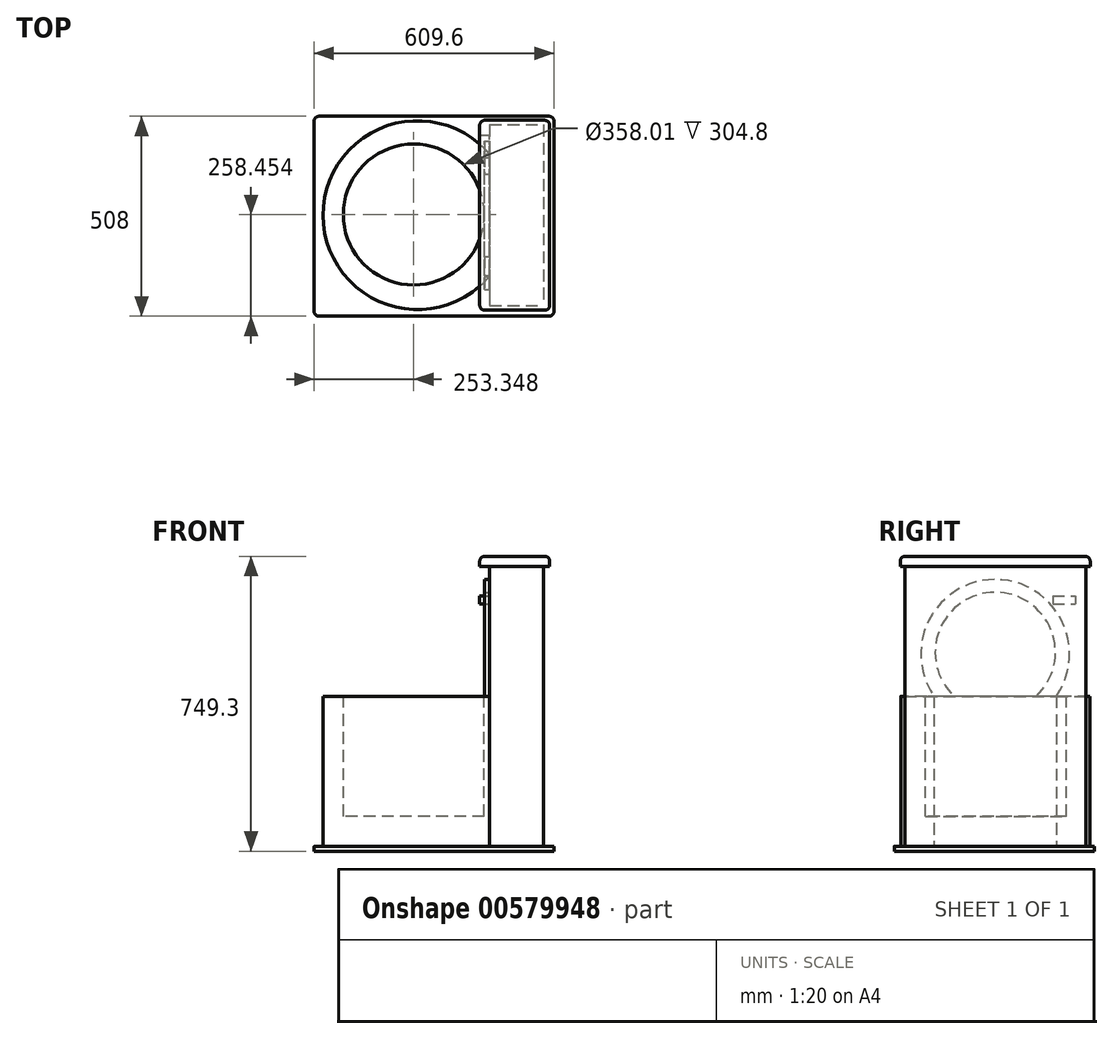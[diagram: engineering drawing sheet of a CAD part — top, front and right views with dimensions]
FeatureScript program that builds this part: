
annotation { "Feature Type Name" : "Feature", "Feature Type Description" : "" }
export const myFeature = defineFeature(function(context is Context, id is Id, definition is map)
    precondition{}
    {
        {
            var Q0;
            Q0=qCreatedBy(makeId("Top.planeOp"),FACE);
            var sketch = newSketch(context, id + "F0", { "sketchPlane" : qUnion([Q0])});
            skLineSegment(sketch, "E0.bottom", {"start": v(-336.58, 285.89) * mm, "end": v(273.02, 285.89) * mm});
            skLineSegment(sketch, "E0.top", {"start": v(-336.58, -222.11) * mm, "end": v(273.02, -222.11) * mm});
            skLineSegment(sketch, "E0.left", {"start": v(-336.58, 285.89) * mm, "end": v(-336.58, -222.11) * mm});
            skLineSegment(sketch, "E0.right", {"start": v(273.02, 285.89) * mm, "end": v(273.02, -222.11) * mm});
            skSolve(sketch);
        }
        {
            var Q0;
            Q0=makeQuery(id+"F0.imprint","IMPRINT",FACE,{"disambiguationData":[TD([[makeQuery(id+"F0.imprint","IMPRINT",EDGE,{"derivedFrom":sQuery(id+"F0.wireOp",EDGE,"E0.bottom")}),-1.0]])]});
            extrude(context, id + "F1", {"entities" : qUnion([Q0]), "depth" : 12.7 * mm, "offsetDistance" : 25.4 * mm});
        }
        {
            var Q0;
            Q0=makeQuery(id+"F1.opExtrude","CAP_FACE",FACE,{"disambiguationData":[OSD([sQuery(id+"F0.wireOp",EDGE,"E0.bottom"),sQuery(id+"F0.wireOp",EDGE,"E0.top"),sQuery(id+"F0.wireOp",EDGE,"E0.left"),sQuery(id+"F0.wireOp",EDGE,"E0.right")])],"isStart":false});
            var sketch = newSketch(context, id + "F2", { "sketchPlane" : qUnion([Q0])});
            skArc(sketch, "E1", {"start": v(109.27, 189.67) * mm, "mid": v(-313.64, 34.5) * mm, "end": v(109.27, -120.68) * mm});
            skPoint(sketch, "E1.first.point", {"position": v(-246.1, 201.36) * mm});
            skPoint(sketch, "E1.second.point", {"position": v(104.1, -126.58) * mm});
            skPoint(sketch, "E1.third.point", {"position": v(-122.1, -200.5) * mm});
            skLineSegment(sketch, "E2.bottom", {"start": v(109.27, 264.4) * mm, "end": v(245.98, 264.4) * mm});
            skLineSegment(sketch, "E2.top", {"start": v(109.27, -195.22) * mm, "end": v(245.98, -195.22) * mm});
            skLineSegment(sketch, "E2.left", {"start": v(109.27, 264.4) * mm, "end": v(109.27, 189.67) * mm});
            skLineSegment(sketch, "E2.right", {"start": v(245.98, 264.4) * mm, "end": v(245.98, -195.22) * mm});
            skLineSegment(sketch, "E3.trimOffspring", {"start": v(109.27, -120.68) * mm, "end": v(109.27, -195.22) * mm});
            skSolve(sketch);
        }
        {
            var Q0;
            Q0 = qSketchRegion(id + "F2", true);
            extrude(context, id + "F3", {"entities" : qUnion([Q0]), "operationType" : NewBodyOperationType.ADD, "depth" : 381 * mm, "offsetDistance" : 25.4 * mm});
        }
        {
            var Q0;
            Q0=makeQuery(id+"F1.opExtrude","SWEPT_EDGE",EDGE,{"disambiguationData":[OSD([sQuery(id+"F0.wireOp",EDGE,"E0.top"),sQuery(id+"F0.wireOp",EDGE,"E0.left")])]});
            var Q1;
            Q1=makeQuery(id+"F1.opExtrude","SWEPT_EDGE",EDGE,{"disambiguationData":[OSD([sQuery(id+"F0.wireOp",EDGE,"E0.top"),sQuery(id+"F0.wireOp",EDGE,"E0.right")])]});
            var Q2;
            Q2=makeQuery(id+"F1.opExtrude","SWEPT_EDGE",EDGE,{"disambiguationData":[OSD([sQuery(id+"F0.wireOp",EDGE,"E0.bottom"),sQuery(id+"F0.wireOp",EDGE,"E0.right")])]});
            var Q3;
            Q3=makeQuery(id+"F1.opExtrude","SWEPT_EDGE",EDGE,{"disambiguationData":[OSD([sQuery(id+"F0.wireOp",EDGE,"E0.bottom"),sQuery(id+"F0.wireOp",EDGE,"E0.left")])]});
            fillet(context, id + "F4", {"entities" : qUnion([Q0, Q1, Q2, Q3]), "radius" : 12.7 * mm, "tangentPropagation" : true, "allowEdgeOverflow" : false});
        }
        {
            var Q0;
            Q0=makeQuery(id+"F3.opExtrude","CAP_FACE",FACE,{"disambiguationData":[OSD([sQuery(id+"F2.wireOp",EDGE,"E1"),sQuery(id+"F2.wireOp",EDGE,"E2.bottom"),sQuery(id+"F2.wireOp",EDGE,"E2.top"),sQuery(id+"F2.wireOp",EDGE,"E2.left"),sQuery(id+"F2.wireOp",EDGE,"E2.right"),sQuery(id+"F2.wireOp",EDGE,"E3.trimOffspring")])],"isStart":false});
            var sketch = newSketch(context, id + "F5", { "sketchPlane" : qUnion([Q0])});
            skCircle(sketch, "E4", {"center": v(-83.23, 36.34) * mm, "radius": 179 * mm});
            skSolve(sketch);
        }
        {
            var Q0;
            Q0 = qSketchRegion(id + "F5", true);
            extrude(context, id + "F6", {"entities" : qUnion([Q0]), "operationType" : NewBodyOperationType.REMOVE, "oppositeDirection" : true, "depth" : 304.8 * mm, "offsetDistance" : 25.4 * mm});
        }
        {
            var Q0;
            Q0=makeQuery(id+"F3.opExtrude","CAP_FACE",FACE,{"disambiguationData":[OSD([sQuery(id+"F2.wireOp",EDGE,"E1"),sQuery(id+"F2.wireOp",EDGE,"E2.bottom"),sQuery(id+"F2.wireOp",EDGE,"E2.top"),sQuery(id+"F2.wireOp",EDGE,"E2.left"),sQuery(id+"F2.wireOp",EDGE,"E2.right"),sQuery(id+"F2.wireOp",EDGE,"E3.trimOffspring")])],"isStart":false});
            var sketch = newSketch(context, id + "F7", { "sketchPlane" : qUnion([Q0])});
            skLineSegment(sketch, "E5.bottom", {"start": v(109.27, 264.4) * mm, "end": v(245.98, 264.4) * mm});
            skLineSegment(sketch, "E5.top", {"start": v(109.27, -195.22) * mm, "end": v(245.98, -195.22) * mm});
            skLineSegment(sketch, "E5.left", {"start": v(109.27, 264.4) * mm, "end": v(109.27, -195.22) * mm});
            skLineSegment(sketch, "E5.right", {"start": v(245.98, 264.4) * mm, "end": v(245.98, -195.22) * mm});
            skSolve(sketch);
        }
        {
            var Q0;
            Q0 = qSketchRegion(id + "F7", true);
            extrude(context, id + "F8", {"entities" : qUnion([Q0]), "operationType" : NewBodyOperationType.ADD, "depth" : 330.2 * mm, "offsetDistance" : 25.4 * mm});
        }
        {
            var Q0;
            Q0=makeQuery(id+"F8.boolean.opBoolean","MERGE",FACE,{"derivedFrom":[makeQuery(id+"F3.opExtrude","SWEPT_FACE",FACE,{"disambiguationData":[OSD([sQuery(id+"F2.wireOp",EDGE,"E2.left")])]}),makeQuery(id+"F3.opExtrude","SWEPT_FACE",FACE,{"disambiguationData":[OSD([sQuery(id+"F2.wireOp",EDGE,"E3.trimOffspring")])]}),makeQuery(id+"F8.opExtrude","SWEPT_FACE",FACE,{"disambiguationData":[OSD([sQuery(id+"F7.wireOp",EDGE,"E5.left")])]})]});
            var sketch = newSketch(context, id + "F9", { "sketchPlane" : qUnion([Q0])});
            skLineSegment(sketch, "E6.bottom", {"start": v(-180.72, 648.78) * mm, "end": v(-237.5, 648.78) * mm});
            skLineSegment(sketch, "E6.top", {"start": v(-180.72, 627.81) * mm, "end": v(-237.5, 627.81) * mm});
            skLineSegment(sketch, "E6.left", {"start": v(-180.72, 648.78) * mm, "end": v(-180.72, 627.81) * mm});
            skLineSegment(sketch, "E6.right", {"start": v(-237.5, 648.78) * mm, "end": v(-237.5, 627.81) * mm});
            skSolve(sketch);
        }
        {
            var Q0;
            Q0 = qSketchRegion(id + "F9", true);
            extrude(context, id + "F10", {"entities" : qUnion([Q0]), "operationType" : NewBodyOperationType.ADD, "depth" : 25.4 * mm, "offsetDistance" : 25.4 * mm});
        }
        {
            var Q0;
            Q0=makeQuery(id+"F8.boolean.opBoolean","MERGE",FACE,{"derivedFrom":[makeQuery(id+"F3.opExtrude","SWEPT_FACE",FACE,{"disambiguationData":[OSD([sQuery(id+"F2.wireOp",EDGE,"E2.left")])]}),makeQuery(id+"F3.opExtrude","SWEPT_FACE",FACE,{"disambiguationData":[OSD([sQuery(id+"F2.wireOp",EDGE,"E3.trimOffspring")])]}),makeQuery(id+"F8.opExtrude","SWEPT_FACE",FACE,{"disambiguationData":[OSD([sQuery(id+"F7.wireOp",EDGE,"E5.left")])]})]});
            var sketch = newSketch(context, id + "F11", { "sketchPlane" : qUnion([Q0])});
            skLineSegment(sketch, "E7", {"start": v(-189.67, 393.7) * mm, "end": v(-138.87, 393.7) * mm});
            skArc(sketch, "E8", {"start": v(120.68, 393.7) * mm, "mid": v(-34.5, 690.42) * mm, "end": v(-189.67, 393.7) * mm});
            skArc(sketch, "E9", {"start": v(69.88, 393.7) * mm, "mid": v(-34.5, 658) * mm, "end": v(-138.87, 393.7) * mm});
            skLineSegment(sketch, "E10.trimOffspring", {"start": v(69.88, 393.7) * mm, "end": v(120.68, 393.7) * mm});
            skSolve(sketch);
        }
        {
            var Q0;
            Q0 = qSketchRegion(id + "F11", true);
            extrude(context, id + "F12", {"entities" : qUnion([Q0]), "operationType" : NewBodyOperationType.ADD, "depth" : 12.7 * mm, "offsetDistance" : 25.4 * mm});
        }
        {
            var Q0;
            Q0=makeQuery(id+"F8.opExtrude","CAP_FACE",FACE,{"disambiguationData":[OSD([sQuery(id+"F7.wireOp",EDGE,"E5.bottom"),sQuery(id+"F7.wireOp",EDGE,"E5.top"),sQuery(id+"F7.wireOp",EDGE,"E5.left"),sQuery(id+"F7.wireOp",EDGE,"E5.right")])],"isStart":false});
            var sketch = newSketch(context, id + "F13", { "sketchPlane" : qUnion([Q0])});
            skLineSegment(sketch, "E11.bottom", {"start": v(84.37, 275.67) * mm, "end": v(262.17, 275.67) * mm});
            skLineSegment(sketch, "E11.top", {"start": v(84.37, -206.93) * mm, "end": v(262.17, -206.93) * mm});
            skLineSegment(sketch, "E11.left", {"start": v(84.37, 275.67) * mm, "end": v(84.37, -206.93) * mm});
            skLineSegment(sketch, "E11.right", {"start": v(262.17, 275.67) * mm, "end": v(262.17, -206.93) * mm});
            skSolve(sketch);
        }
        {
            var Q0;
            Q0 = qSketchRegion(id + "F13", true);
            extrude(context, id + "F14", {"entities" : qUnion([Q0]), "operationType" : NewBodyOperationType.ADD, "depth" : 25.4 * mm, "offsetDistance" : 25.4 * mm});
        }
        {
            var Q0;
            Q0=makeQuery(id+"F14.opExtrude","SWEPT_EDGE",EDGE,{"disambiguationData":[OSD([sQuery(id+"F13.wireOp",EDGE,"E11.top"),sQuery(id+"F13.wireOp",EDGE,"E11.left")])]});
            var Q1;
            Q1=makeQuery(id+"F14.opExtrude","CAP_EDGE",EDGE,{"disambiguationData":[OSD([sQuery(id+"F13.wireOp",EDGE,"E11.left")])],"isStart":false});
            var Q2;
            Q2=makeQuery(id+"F14.opExtrude","SWEPT_EDGE",EDGE,{"disambiguationData":[OSD([sQuery(id+"F13.wireOp",EDGE,"E11.top"),sQuery(id+"F13.wireOp",EDGE,"E11.right")])]});
            var Q3;
            Q3=makeQuery(id+"F14.opExtrude","CAP_EDGE",EDGE,{"disambiguationData":[OSD([sQuery(id+"F13.wireOp",EDGE,"E11.top")])],"isStart":false});
            var Q4;
            Q4=makeQuery(id+"F14.opExtrude","CAP_EDGE",EDGE,{"disambiguationData":[OSD([sQuery(id+"F13.wireOp",EDGE,"E11.right")])],"isStart":false});
            var Q5;
            Q5=makeQuery(id+"F14.opExtrude","SWEPT_EDGE",EDGE,{"disambiguationData":[OSD([sQuery(id+"F13.wireOp",EDGE,"E11.bottom"),sQuery(id+"F13.wireOp",EDGE,"E11.right")])]});
            var Q6;
            Q6=makeQuery(id+"F14.opExtrude","SWEPT_EDGE",EDGE,{"disambiguationData":[OSD([sQuery(id+"F13.wireOp",EDGE,"E11.bottom"),sQuery(id+"F13.wireOp",EDGE,"E11.left")])]});
            var Q7;
            Q7=makeQuery(id+"F14.opExtrude","CAP_EDGE",EDGE,{"disambiguationData":[OSD([sQuery(id+"F13.wireOp",EDGE,"E11.bottom")])],"isStart":false});
            fillet(context, id + "F15", {"entities" : qUnion([Q0, Q1, Q2, Q3, Q4, Q5, Q6, Q7]), "radius" : 12.7 * mm, "tangentPropagation" : true, "allowEdgeOverflow" : false});
        }
    });
